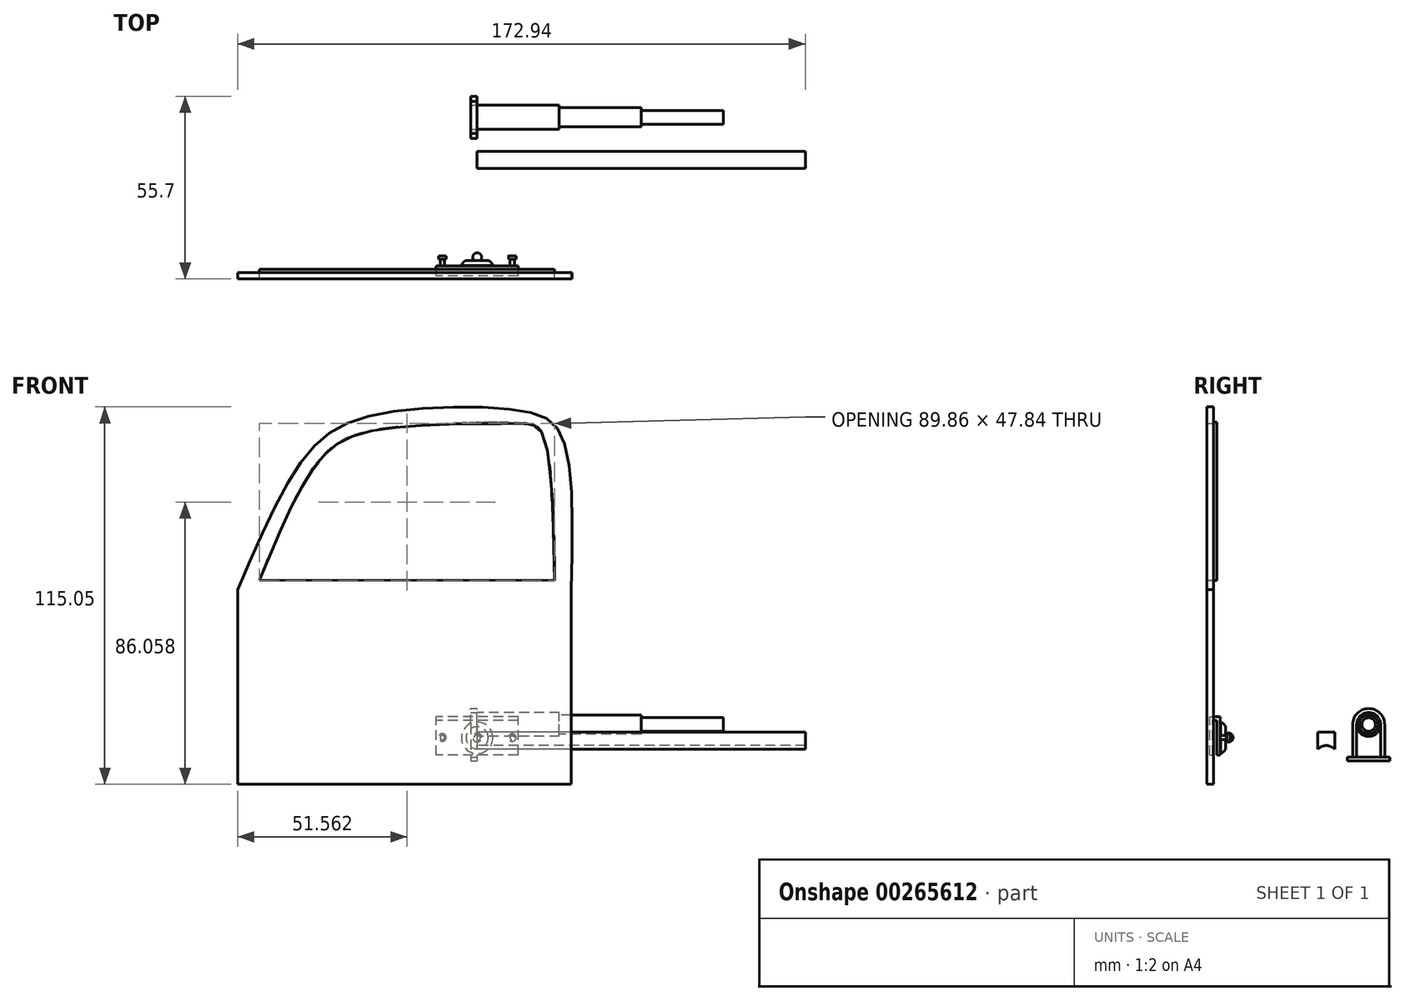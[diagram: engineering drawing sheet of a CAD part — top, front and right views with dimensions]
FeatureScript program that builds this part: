
annotation { "Feature Type Name" : "Feature", "Feature Type Description" : "" }
export const myFeature = defineFeature(function(context is Context, id is Id, definition is map)
    precondition{}
    {
        {
            var Q0;
            Q0=qCreatedBy(makeId("Front.planeOp"),FACE);
            var sketch = newSketch(context, id + "F0", { "sketchPlane" : qUnion([Q0])});
            skLineSegment(sketch, "E0.bottom", {"start": v(28.62, -81.37) * mm, "end": v(-72.94, -81.37) * mm});
            skLineSegment(sketch, "E0.left", {"start": v(28.62, -81.37) * mm, "end": v(28.62, -22.05) * mm});
            skLineSegment(sketch, "E0.right", {"start": v(-72.94, -81.37) * mm, "end": v(-72.94, -22.05) * mm});
            skFitSpline(sketch, "E1", {"points": [v(-72.94, -22.05) * mm, v(-52.29, 18.69) * mm, v(-31.26, 31.27) * mm, v(13.98, 32.4) * mm, v(25.8, 24.7) * mm, v(28.62, -22.05) * mm], "startDerivative": vector(85.44, 201.79) * mm, "endDerivative": vector(-6.45, -241.46) * mm});
            skFitSpline(sketch, "E2", {"points": [v(-66.3, -19.04) * mm, v(-48.72, 16.62) * mm, v(-31.26, 26.57) * mm, v(11.54, 28.64) * mm, v(20.36, 24.32) * mm, v(23.55, -19.23) * mm, v(23.55, -19.42) * mm], "startDerivative": vector(74.67, 181.05) * mm, "endDerivative": vector(0.05, -3.93) * mm});
            skLineSegment(sketch, "E3", {"start": v(-66.3, -19.04) * mm, "end": v(23.55, -19.23) * mm});
            skSolve(sketch);
        }
        {
            var Q0;
            Q0=makeQuery(id+"F0.imprint","IMPRINT",FACE,{"disambiguationData":[TD([[makeQuery(id+"F0.imprint","IMPRINT",EDGE,{"derivedFrom":sQuery(id+"F0.wireOp",EDGE,"E0.bottom")}),-1.0]])]});
            var Q1;
            Q1=makeQuery(id+"F0.imprint","IMPRINT",FACE,{"disambiguationData":[TD([[makeQuery(id+"F0.imprint","IMPRINT",EDGE,{"derivedFrom":sQuery(id+"F0.wireOp",EDGE,"UIrI5waD-Pjwz-Hmjb-fkDX-1jexeotdMPTl.bottom")}),1.0]])]});
            var Q2;
            Q2=qConstructionFilter(qBodyType(qCreatedBy(id+"F0",EDGE),BodyType.WIRE),ConstructionObject.NO);
            extrude(context, id + "F1", {"entities" : qUnion([Q0, Q1]), "surfaceEntities" : qUnion([Q2]), "depth" : 2 * mm});
        }
        {
            var Q0;
            Q0=makeQuery(id+"F1.opExtrude","CAP_FACE",FACE,{"disambiguationData":[OSD([sQuery(id+"F0.wireOp",EDGE,"E0.bottom"),sQuery(id+"F0.wireOp",EDGE,"E0.left"),sQuery(id+"F0.wireOp",EDGE,"E0.right"),sQuery(id+"F0.wireOp",EDGE,"E1"),sQuery(id+"F0.wireOp",EDGE,"E2"),sQuery(id+"F0.wireOp",EDGE,"E3")])],"isStart":true});
            var sketch = newSketch(context, id + "F2", { "sketchPlane" : qUnion([Q0])});
            skLineSegment(sketch, "E4", {"start": v(66.3, -19.04) * mm, "end": v(-23.55, -19.23) * mm});
            skFitSpline(sketch, "E5", {"points": [v(-23.55, -19.23) * mm, v(-22, 16.14) * mm, v(-19.49, 26.26) * mm, v(-14.23, 28.67) * mm, v(29.92, 26.8) * mm, v(44.38, 21.19) * mm, v(55.39, 5.68) * mm, v(63.63, -12.57) * mm, v(66.3, -19.04) * mm], "startDerivative": vector(4.8, 225.63) * mm, "endDerivative": vector(30.03, -71) * mm});
            skPoint(sketch, "E6.start.orphan", {"position": v(57.04, -62.16) * mm});
            skSolve(sketch);
        }
        {
            var Q0;
            Q0=qSketchRegion(id+"F2",true);
            extrude(context, id + "F3", {"entities" : qUnion([Q0]), "depth" : 1 * mm});
        }
        {
            var Q0;
            Q0=qCreatedBy(makeId("Right.planeOp"),FACE);
            var sketch = newSketch(context, id + "F4", { "sketchPlane" : qUnion([Q0])});
            skLineSegment(sketch, "E7.bottom", {"start": v(-1.09, -72.45) * mm, "end": v(-0.22, -72.45) * mm});
            skLineSegment(sketch, "E7.top", {"start": v(-1.09, -60.77) * mm, "end": v(2.05, -60.77) * mm});
            skLineSegment(sketch, "E7.left", {"start": v(-1.09, -72.45) * mm, "end": v(-1.09, -60.77) * mm});
            skLineSegment(sketch, "E7.right", {"start": v(2.05, -72.45) * mm, "end": v(2.05, -60.77) * mm});
            skLineSegment(sketch, "E8", {"start": v(-0.22, -72.45) * mm, "end": v(-0.22, -61.9) * mm});
            skLineSegment(sketch, "E9", {"start": v(-0.22, -61.9) * mm, "end": v(1.02, -61.9) * mm});
            skLineSegment(sketch, "E10", {"start": v(1.02, -61.9) * mm, "end": v(1.02, -72.45) * mm});
            skLineSegment(sketch, "E11.trimOffspring", {"start": v(1.02, -72.45) * mm, "end": v(2.05, -72.45) * mm});
            skSolve(sketch);
        }
        {
            var Q0;
            Q0=qSketchRegion(id+"F4",true);
            extrude(context, id + "F5", {"entities" : qUnion([Q0]), "endBound" : BoundingType.SYMMETRIC, "depth" : 25 * mm});
        }
        {
            var Q0;
            Q0=makeQuery(id+"F5.opExtrude","SWEPT_FACE",FACE,{"disambiguationData":[OSD([sQuery(id+"F4.wireOp",EDGE,"E7.right")])]});
            var sketch = newSketch(context, id + "F6", { "sketchPlane" : qUnion([Q0])});
            skCircle(sketch, "E12", {"center": v(-10.7, -67.1) * mm, "radius": 0.67 * mm});
            skCircle(sketch, "E13", {"center": v(10.58, -67.1) * mm, "radius": 0.68 * mm});
            skSolve(sketch);
        }
        {
            var Q0;
            Q0=qSketchRegion(id+"F6",true);
            extrude(context, id + "F7", {"entities" : qUnion([Q0]), "operationType" : NewBodyOperationType.ADD, "depth" : 2 * mm});
        }
        {
            var Q0;
            Q0=makeQuery(id+"F7.opExtrude","CAP_FACE",FACE,{"disambiguationData":[OSD([sQuery(id+"F6.wireOp",EDGE,"E12")])],"isStart":false});
            var sketch = newSketch(context, id + "F8", { "sketchPlane" : qUnion([Q0])});
            skCircle(sketch, "E14", {"center": v(-10.7, -67.1) * mm, "radius": 1.15 * mm});
            skCircle(sketch, "E15", {"center": v(10.6, -67.07) * mm, "radius": 1.15 * mm});
            skSolve(sketch);
        }
        {
            var Q0;
            Q0=qSketchRegion(id+"F8",true);
            extrude(context, id + "F9", {"entities" : qUnion([Q0]), "operationType" : NewBodyOperationType.ADD, "depth" : 1 * mm});
        }
        {
            var Q0;
            Q0=qCreatedBy(makeId("Right.planeOp"),FACE);
            var sketch = newSketch(context, id + "F10", { "sketchPlane" : qUnion([Q0])});
            skLineSegment(sketch, "E16.bottom", {"start": v(2.07, -62.39) * mm, "end": v(2.13, -62.39) * mm});
            skLineSegment(sketch, "E16.top", {"start": v(2.07, -67.18) * mm, "end": v(3.69, -67.18) * mm});
            skLineSegment(sketch, "E16.left", {"start": v(2.07, -62.39) * mm, "end": v(2.07, -67.18) * mm});
            skLineSegment(sketch, "E16.right", {"start": v(3.69, -63.81) * mm, "end": v(3.69, -67.18) * mm});
            skLineSegment(sketch, "E17", {"start": v(2.07, -67.18) * mm, "end": v(6.73, -67.18) * mm, "construction": true});
            skArc(sketch, "E18", {"start": v(3.69, -63.81) * mm, "mid": v(3.07, -62.93) * mm, "end": v(2.13, -62.39) * mm});
            skPoint(sketch, "E19", {"position": v(2.07, -64.78) * mm});
            skSolve(sketch);
        }
        {
            var Q0;
            Q0=makeQuery(id+"F10.imprint","IMPRINT",FACE,{"disambiguationData":[TD([[makeQuery(id+"F10.imprint","IMPRINT",EDGE,{"derivedFrom":sQuery(id+"F10.wireOp",EDGE,"E16.bottom")}),-1.0]])]});
            var Q1;
            Q1=sQuery(id+"F10.wireOp",EDGE,"E17");
            revolve(context, id + "F11", {"entities" : qUnion([Q0]), "axis" : qUnion([Q1]), "revolveType" : RevolveType.FULL});
        }
        {
            var Q0;
            Q0=qCreatedBy(makeId("Right.planeOp"),FACE);
            var sketch = newSketch(context, id + "F12", { "sketchPlane" : qUnion([Q0])});
            skArc(sketch, "E20", {"start": v(6, -67.1) * mm, "mid": v(4.64, -65.75) * mm, "end": v(3.3, -67.1) * mm});
            skLineSegment(sketch, "E21", {"start": v(2.6, -67.1) * mm, "end": v(7.1, -67.1) * mm, "construction": true});
            skLineSegment(sketch, "E22", {"start": v(3.3, -67.1) * mm, "end": v(6, -67.1) * mm});
            skSolve(sketch);
        }
        {
            var Q0;
            Q0=makeQuery(id+"F12.imprint","IMPRINT",FACE,{"disambiguationData":[TD([[makeQuery(id+"F12.imprint","IMPRINT",EDGE,{"derivedFrom":sQuery(id+"F12.wireOp",EDGE,"E20")}),1.0]])]});
            var Q1;
            Q1=sQuery(id+"F12.wireOp",EDGE,"E21");
            revolve(context, id + "F13", {"operationType" : NewBodyOperationType.ADD, "entities" : qUnion([Q0]), "axis" : qUnion([Q1]), "revolveType" : RevolveType.FULL});
        }
        {
            var Q0;
            Q0=qCreatedBy(makeId("Right.planeOp"),FACE);
            var sketch = newSketch(context, id + "F14", { "sketchPlane" : qUnion([Q0])});
            skLineSegment(sketch, "E23.bottom", {"start": v(31.76, -65.44) * mm, "end": v(36.96, -65.44) * mm});
            skLineSegment(sketch, "E23.left", {"start": v(31.76, -65.44) * mm, "end": v(31.76, -70.68) * mm});
            skLineSegment(sketch, "E23.right", {"start": v(36.96, -65.44) * mm, "end": v(36.96, -70.68) * mm});
            skPoint(sketch, "E23.middle", {"position": v(34.36, -68.06) * mm});
            skArc(sketch, "E24", {"start": v(36.96, -70.68) * mm, "mid": v(34.36, -69.56) * mm, "end": v(31.76, -70.68) * mm});
            skPoint(sketch, "E24.centerSnap0", {"position": v(34.36, -70.68) * mm});
            skSolve(sketch);
        }
        {
            var Q0;
            Q0 = qSketchRegion(id + "F14", true);
            extrude(context, id + "F15", {"entities" : qUnion([Q0]), "depth" : 100 * mm});
        }
        {
            var Q0;
            Q0=qCreatedBy(makeId("Right.planeOp"),FACE);
            var sketch = newSketch(context, id + "F16", { "sketchPlane" : qUnion([Q0])});
            skCircle(sketch, "E25", {"center": v(47.3, -63.13) * mm, "radius": 3.65 * mm});
            skSolve(sketch);
        }
        {
            var Q0;
            Q0 = qSketchRegion(id + "F16", true);
            extrude(context, id + "F17", {"entities" : qUnion([Q0]), "depth" : 25 * mm});
        }
        {
            var Q0;
            Q0=makeQuery(id+"F17.opExtrude","CAP_FACE",FACE,{"disambiguationData":[OSD([sQuery(id+"F16.wireOp",EDGE,"E25")])],"isStart":false});
            var sketch = newSketch(context, id + "F18", { "sketchPlane" : qUnion([Q0])});
            skCircle(sketch, "E26", {"center": v(47.3, -63.13) * mm, "radius": 2.92 * mm});
            skSolve(sketch);
        }
        {
            var Q0;
            Q0=makeQuery(id+"F18.imprint","IMPRINT",FACE,{"disambiguationData":[TD([[makeQuery(id+"F18.imprint","IMPRINT",EDGE,{"derivedFrom":sQuery(id+"F18.wireOp",EDGE,"E26")}),1.0]])]});
            extrude(context, id + "F19", {"entities" : qUnion([Q0]), "operationType" : NewBodyOperationType.ADD, "depth" : 25 * mm});
        }
        {
            var Q0;
            Q0=makeQuery(id+"F19.opExtrude","CAP_FACE",FACE,{"disambiguationData":[OSD([sQuery(id+"F18.wireOp",EDGE,"E26")])],"isStart":false});
            var sketch = newSketch(context, id + "F20", { "sketchPlane" : qUnion([Q0])});
            skCircle(sketch, "E27", {"center": v(47.3, -63.13) * mm, "radius": 2.08 * mm});
            skSolve(sketch);
        }
        {
            var Q0;
            Q0 = qSketchRegion(id + "F20", true);
            extrude(context, id + "F21", {"entities" : qUnion([Q0]), "operationType" : NewBodyOperationType.ADD, "depth" : 25 * mm});
        }
        {
            var Q0;
            Q0=makeQuery(id+"F17.opExtrude","CAP_FACE",FACE,{"disambiguationData":[OSD([sQuery(id+"F16.wireOp",EDGE,"E25")])],"isStart":true});
            var sketch = newSketch(context, id + "F22", { "sketchPlane" : qUnion([Q0])});
            skArc(sketch, "E28", {"start": v(-42.43, -63.13) * mm, "mid": v(-47.3, -58.26) * mm, "end": v(-52.17, -63.13) * mm});
            skLineSegment(sketch, "E29.left", {"start": v(-52.17, -63.13) * mm, "end": v(-52.17, -73.09) * mm});
            skLineSegment(sketch, "E29.right", {"start": v(-42.43, -63.13) * mm, "end": v(-42.43, -73.09) * mm});
            skLineSegment(sketch, "E30", {"start": v(-50.95, -63.13) * mm, "end": v(-50.95, -73.09) * mm});
            skLineSegment(sketch, "E31", {"start": v(-43.65, -63.13) * mm, "end": v(-43.65, -73.09) * mm});
            skArc(sketch, "E32", {"start": v(-43.65, -63.13) * mm, "mid": v(-47.3, -59.48) * mm, "end": v(-50.95, -63.13) * mm});
            skLineSegment(sketch, "E33.bottom", {"start": v(-53.7, -73.09) * mm, "end": v(-40.84, -73.09) * mm});
            skLineSegment(sketch, "E33.top", {"start": v(-53.7, -74.22) * mm, "end": v(-40.84, -74.22) * mm});
            skLineSegment(sketch, "E33.left", {"start": v(-53.7, -73.09) * mm, "end": v(-53.7, -74.22) * mm});
            skLineSegment(sketch, "E33.right", {"start": v(-40.84, -73.09) * mm, "end": v(-40.84, -74.22) * mm});
            skSolve(sketch);
        }
        {
            var Q0;
            Q0=makeQuery(id+"F22.imprint","IMPRINT",FACE,{"disambiguationData":[TD([[makeQuery(id+"F22.imprint","IMPRINT",EDGE,{"derivedFrom":sQuery(id+"F22.wireOp",EDGE,"E28")}),1.0]])]});
            var Q1;
            Q1=makeQuery(id+"F22.imprint","IMPRINT",FACE,{"disambiguationData":[TD([[makeQuery(id+"F22.imprint","IMPRINT",EDGE,{"derivedFrom":sQuery(id+"F22.wireOp",EDGE,"E29.top")}),1.0]])]});
            var Q2;
            Q2=makeQuery(id+"F22.imprint","IMPRINT",FACE,{"disambiguationData":[TD([[makeQuery(id+"F22.imprint","IMPRINT",EDGE,{"derivedFrom":sQuery(id+"F22.wireOp",EDGE,"f6835785-e086-4e4e-9719-fc25478ede25.trimOffspring")}),1.0]])]});
            extrude(context, id + "F23", {"entities" : qUnion([Q0, Q1, Q2]), "depth" : 2 * mm});
        }
        {
            var Q0;
            {var subQ8=sQuery(id+"F22.wireOp",EDGE,"E33.left");Q0=makeQuery(id+"F22.imprint","IMPRINT",FACE,{"disambiguationData":[TD([[makeQuery(id+"F22.imprint","IMPRINT",EDGE,{"derivedFrom":subQ8}),1.0]])]});}
            extrude(context, id + "F24", {"entities" : qUnion([Q0]), "depth" : 2 * mm});
        }
    });
